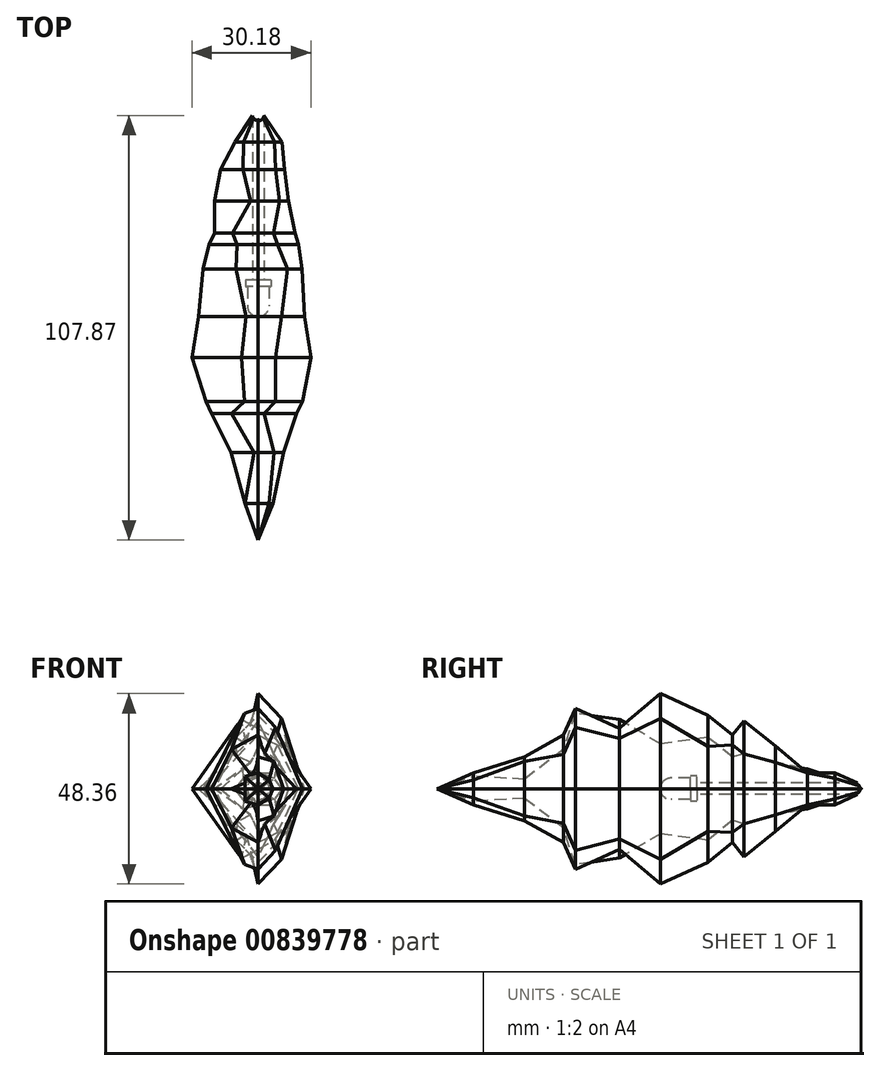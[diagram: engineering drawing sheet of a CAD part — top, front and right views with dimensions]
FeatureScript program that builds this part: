
annotation { "Feature Type Name" : "Feature", "Feature Type Description" : "" }
export const myFeature = defineFeature(function(context is Context, id is Id, definition is map)
    precondition{}
    {
        {
            var Q0;
            Q0=qCreatedBy(makeId("Right.planeOp"),FACE);
            var sketch = newSketch(context, id + "F0", { "sketchPlane" : qUnion([Q0])});
            skLineSegment(sketch, "E0", {"start": v(-34.53, 8.11) * mm, "end": v(-24.64, 13.67) * mm});
            skLineSegment(sketch, "E1", {"start": v(-24.64, 13.67) * mm, "end": v(-21.55, 20.44) * mm});
            skLineSegment(sketch, "E2", {"start": v(-21.55, 20.44) * mm, "end": v(-10.37, 15.33) * mm});
            skLineSegment(sketch, "E3", {"start": v(-10.37, 15.33) * mm, "end": v(0, 24.18) * mm});
            skLineSegment(sketch, "E4", {"start": v(0, 24.18) * mm, "end": v(12.06, 18.66) * mm});
            skLineSegment(sketch, "E5", {"start": v(12.06, 18.66) * mm, "end": v(18.3, 13.67) * mm});
            skLineSegment(sketch, "E6", {"start": v(18.3, 13.67) * mm, "end": v(21.2, 17.3) * mm});
            skLineSegment(sketch, "E7", {"start": v(21.2, 17.3) * mm, "end": v(29.3, 10.81) * mm});
            skLineSegment(sketch, "E8", {"start": v(-34.53, 8.11) * mm, "end": v(-47.5, 4.06) * mm});
            skLineSegment(sketch, "E9", {"start": v(-47.5, 4.06) * mm, "end": v(-56.78, 0) * mm});
            skLineSegment(sketch, "E10", {"start": v(44.35, 4.06) * mm, "end": v(53.22, 0) * mm});
            skLineSegment(sketch, "E11", {"start": v(29.3, 10.81) * mm, "end": v(37.37, 4.06) * mm});
            skLineSegment(sketch, "E12", {"start": v(-56.78, 0) * mm, "end": v(53.22, 0) * mm});
            skLineSegment(sketch, "E13", {"start": v(44.35, 4.06) * mm, "end": v(37.37, 4.06) * mm});
            skSolve(sketch);
        }
        {
            var Q0;
            Q0=sQuery(id+"F0.wireOp",VERTEX,"E10.start");
            var Q1;
            Q1=sQuery(id+"F0.wireOp",EDGE,"E12");
            cPlane(context, id + "F1", {"entities" : qUnion([Q0, Q1]), "cplaneType" : CPlaneType.LINE_POINT, "offset" : 25 * mm, "width" : 150 * mm, "height" : 150 * mm});
        }
        {
            var Q0;
            Q0=sQuery(id+"F0.wireOp",VERTEX,"E11.end");
            var Q1;
            Q1=sQuery(id+"F0.wireOp",EDGE,"E12");
            cPlane(context, id + "F2", {"entities" : qUnion([Q0, Q1]), "cplaneType" : CPlaneType.LINE_POINT, "offset" : 25 * mm, "width" : 150 * mm, "height" : 150 * mm});
        }
        {
            var Q0;
            Q0=sQuery(id+"F0.wireOp",VERTEX,"E7.end");
            var Q1;
            Q1=sQuery(id+"F0.wireOp",EDGE,"E12");
            cPlane(context, id + "F3", {"entities" : qUnion([Q0, Q1]), "cplaneType" : CPlaneType.LINE_POINT, "offset" : 25 * mm, "width" : 150 * mm, "height" : 150 * mm});
        }
        {
            var Q0;
            Q0=sQuery(id+"F0.wireOp",VERTEX,"E6.end");
            var Q1;
            Q1=sQuery(id+"F0.wireOp",EDGE,"E12");
            cPlane(context, id + "F4", {"entities" : qUnion([Q0, Q1]), "cplaneType" : CPlaneType.LINE_POINT, "offset" : 25 * mm, "width" : 150 * mm, "height" : 150 * mm});
        }
        {
            var Q0;
            Q0=sQuery(id+"F0.wireOp",VERTEX,"E5.end");
            var Q1;
            Q1=sQuery(id+"F0.wireOp",EDGE,"E12");
            cPlane(context, id + "F5", {"entities" : qUnion([Q0, Q1]), "cplaneType" : CPlaneType.LINE_POINT, "offset" : 25 * mm, "width" : 150 * mm, "height" : 150 * mm});
        }
        {
            var Q0;
            Q0=sQuery(id+"F0.wireOp",VERTEX,"E4.end");
            var Q1;
            Q1=sQuery(id+"F0.wireOp",EDGE,"E12");
            cPlane(context, id + "F6", {"entities" : qUnion([Q0, Q1]), "cplaneType" : CPlaneType.LINE_POINT, "offset" : 25 * mm, "width" : 150 * mm, "height" : 150 * mm});
        }
        {
            var Q0;
            Q0=sQuery(id+"F0.wireOp",VERTEX,"E3.end");
            var Q1;
            Q1=sQuery(id+"F0.wireOp",EDGE,"E12");
            cPlane(context, id + "F7", {"entities" : qUnion([Q0, Q1]), "cplaneType" : CPlaneType.LINE_POINT, "offset" : 25 * mm, "width" : 150 * mm, "height" : 150 * mm});
        }
        {
            var Q0;
            Q0=sQuery(id+"F0.wireOp",VERTEX,"E2.end");
            var Q1;
            Q1=sQuery(id+"F0.wireOp",EDGE,"E12");
            cPlane(context, id + "F8", {"entities" : qUnion([Q0, Q1]), "cplaneType" : CPlaneType.LINE_POINT, "offset" : 25 * mm, "width" : 150 * mm, "height" : 150 * mm});
        }
        {
            var Q0;
            Q0=sQuery(id+"F0.wireOp",VERTEX,"E1.end");
            var Q1;
            Q1=sQuery(id+"F0.wireOp",EDGE,"E12");
            cPlane(context, id + "F9", {"entities" : qUnion([Q0, Q1]), "cplaneType" : CPlaneType.LINE_POINT, "offset" : 25 * mm, "width" : 150 * mm, "height" : 150 * mm});
        }
        {
            var Q0;
            Q0=sQuery(id+"F0.wireOp",VERTEX,"E0.end");
            var Q1;
            Q1=sQuery(id+"F0.wireOp",EDGE,"E12");
            cPlane(context, id + "F10", {"entities" : qUnion([Q0, Q1]), "cplaneType" : CPlaneType.LINE_POINT, "offset" : 25 * mm, "width" : 150 * mm, "height" : 150 * mm});
        }
        {
            var Q0;
            Q0=sQuery(id+"F0.wireOp",VERTEX,"E0.start");
            var Q1;
            Q1=sQuery(id+"F0.wireOp",EDGE,"E12");
            cPlane(context, id + "F11", {"entities" : qUnion([Q0, Q1]), "cplaneType" : CPlaneType.LINE_POINT, "offset" : 25 * mm, "width" : 150 * mm, "height" : 150 * mm});
        }
        {
            var Q0;
            Q0=sQuery(id+"F0.wireOp",VERTEX,"E8.end");
            var Q1;
            Q1=sQuery(id+"F0.wireOp",EDGE,"E12");
            cPlane(context, id + "F12", {"entities" : qUnion([Q0, Q1]), "cplaneType" : CPlaneType.LINE_POINT, "offset" : 25 * mm, "width" : 150 * mm, "height" : 150 * mm});
        }
        {
            var Q0;
            Q0=qCreatedBy(id+"F1.planeOp",FACE);
            var sketch = newSketch(context, id + "F13", { "sketchPlane" : qUnion([Q0])});
            skPoint(sketch, "E14.0", {"position": v(0, 4.06) * mm});
            skLineSegment(sketch, "E15", {"start": v(0, 4.06) * mm, "end": v(3.8, 2.78) * mm});
            skLineSegment(sketch, "E16", {"start": v(3.8, 2.78) * mm, "end": v(5.94, 0) * mm});
            skLineSegment(sketch, "E17", {"start": v(5.94, 0) * mm, "end": v(-6.04, 0) * mm});
            skLineSegment(sketch, "E18", {"start": v(-6.04, 0) * mm, "end": v(-4.09, 2.6) * mm});
            skLineSegment(sketch, "E19", {"start": v(-4.09, 2.6) * mm, "end": v(0, 4.06) * mm});
            skSolve(sketch);
        }
        {
            var Q0;
            Q0=qCreatedBy(id+"F2.planeOp",FACE);
            var sketch = newSketch(context, id + "F14", { "sketchPlane" : qUnion([Q0])});
            skPoint(sketch, "E20.0", {"position": v(0, 4.06) * mm});
            skLineSegment(sketch, "E21", {"start": v(0, 4.06) * mm, "end": v(-4.45, 4.06) * mm});
            skLineSegment(sketch, "E22", {"start": v(-4.45, 4.06) * mm, "end": v(-6.68, 0) * mm});
            skLineSegment(sketch, "E23", {"start": v(-6.68, 0) * mm, "end": v(9.54, 0) * mm});
            skLineSegment(sketch, "E24", {"start": v(9.54, 0) * mm, "end": v(3.9, 5.05) * mm});
            skLineSegment(sketch, "E25", {"start": v(3.9, 5.05) * mm, "end": v(0, 4.06) * mm});
            skSolve(sketch);
        }
        {
            var Q0;
            Q0=qCreatedBy(id+"F3.planeOp",FACE);
            var sketch = newSketch(context, id + "F15", { "sketchPlane" : qUnion([Q0])});
            skPoint(sketch, "E26", {"position": v(0, 10.87) * mm});
            skLineSegment(sketch, "E27", {"start": v(-7.66, 0) * mm, "end": v(-5.4, 6.67) * mm});
            skLineSegment(sketch, "E28", {"start": v(-5.4, 6.67) * mm, "end": v(0, 10.87) * mm});
            skLineSegment(sketch, "E29", {"start": v(0, 10.87) * mm, "end": v(1.92, 6.67) * mm});
            skLineSegment(sketch, "E30", {"start": v(1.92, 6.67) * mm, "end": v(11.06, 0) * mm});
            skLineSegment(sketch, "E31", {"start": v(11.06, 0) * mm, "end": v(-7.66, 0) * mm});
            skSolve(sketch);
        }
        {
            var Q0;
            Q0=qCreatedBy(id+"F4.planeOp",FACE);
            var sketch = newSketch(context, id + "F16", { "sketchPlane" : qUnion([Q0])});
            skPoint(sketch, "E32.0", {"position": v(0, 17.3) * mm});
            skLineSegment(sketch, "E33", {"start": v(-9.31, 0) * mm, "end": v(-3.87, 8.9) * mm});
            skLineSegment(sketch, "E34", {"start": v(-3.87, 8.9) * mm, "end": v(0, 17.3) * mm});
            skLineSegment(sketch, "E35", {"start": v(0, 17.3) * mm, "end": v(6.54, 8.9) * mm});
            skLineSegment(sketch, "E36", {"start": v(6.54, 8.9) * mm, "end": v(11.15, 0) * mm});
            skLineSegment(sketch, "E37", {"start": v(11.15, 0) * mm, "end": v(-9.31, 0) * mm});
            skSolve(sketch);
        }
        {
            var Q0;
            Q0=qCreatedBy(id+"F5.planeOp",FACE);
            var sketch = newSketch(context, id + "F17", { "sketchPlane" : qUnion([Q0])});
            skPoint(sketch, "E38.0", {"position": v(0, 13.67) * mm});
            skLineSegment(sketch, "E39", {"start": v(0, 13.67) * mm, "end": v(-4.93, 11.1) * mm});
            skLineSegment(sketch, "E40", {"start": v(-4.93, 11.1) * mm, "end": v(-10.2, 0) * mm});
            skLineSegment(sketch, "E41", {"start": v(-10.2, 0) * mm, "end": v(12.55, 0) * mm});
            skLineSegment(sketch, "E42", {"start": v(12.55, 0) * mm, "end": v(5.43, 8.08) * mm});
            skLineSegment(sketch, "E43", {"start": v(5.43, 8.08) * mm, "end": v(0, 13.67) * mm});
            skSolve(sketch);
        }
        {
            var Q0;
            Q0=qCreatedBy(id+"F6.planeOp",FACE);
            var sketch = newSketch(context, id + "F18", { "sketchPlane" : qUnion([Q0])});
            skPoint(sketch, "E44.0", {"position": v(0, 18.66) * mm});
            skLineSegment(sketch, "E45", {"start": v(0, 18.66) * mm, "end": v(-7.43, 10.78) * mm});
            skLineSegment(sketch, "E46", {"start": v(-7.43, 10.78) * mm, "end": v(-11.12, 0) * mm});
            skLineSegment(sketch, "E47", {"start": v(-11.12, 0) * mm, "end": v(14.03, 0) * mm});
            skLineSegment(sketch, "E48", {"start": v(14.03, 0) * mm, "end": v(5.59, 13.07) * mm});
            skLineSegment(sketch, "E49", {"start": v(5.59, 13.07) * mm, "end": v(0, 18.66) * mm});
            skSolve(sketch);
        }
        {
            var Q0;
            Q0=qCreatedBy(id+"F7.planeOp",FACE);
            var sketch = newSketch(context, id + "F19", { "sketchPlane" : qUnion([Q0])});
            skPoint(sketch, "E50.0", {"position": v(0, 24.18) * mm});
            skLineSegment(sketch, "E51", {"start": v(0, 24.18) * mm, "end": v(-5.97, 17.9) * mm});
            skLineSegment(sketch, "E52", {"start": v(-5.97, 17.9) * mm, "end": v(-11.7, 0) * mm});
            skLineSegment(sketch, "E53", {"start": v(-11.7, 0) * mm, "end": v(15.17, 0) * mm});
            skLineSegment(sketch, "E54", {"start": v(15.17, 0) * mm, "end": v(3.05, 11.41) * mm});
            skLineSegment(sketch, "E55", {"start": v(3.05, 11.41) * mm, "end": v(0, 24.18) * mm});
            skSolve(sketch);
        }
        {
            var Q0;
            Q0=qCreatedBy(id+"F8.planeOp",FACE);
            var sketch = newSketch(context, id + "F20", { "sketchPlane" : qUnion([Q0])});
            skPoint(sketch, "E56.0", {"position": v(0, 15.33) * mm});
            skLineSegment(sketch, "E57", {"start": v(0, 15.33) * mm, "end": v(-4.33, 12.79) * mm});
            skLineSegment(sketch, "E58", {"start": v(-4.33, 12.79) * mm, "end": v(-13.36, 0) * mm});
            skLineSegment(sketch, "E59", {"start": v(-13.36, 0) * mm, "end": v(16.82, 0) * mm});
            skLineSegment(sketch, "E60", {"start": v(16.82, 0) * mm, "end": v(4.27, 17.61) * mm});
            skLineSegment(sketch, "E61", {"start": v(4.27, 17.61) * mm, "end": v(0, 15.33) * mm});
            skSolve(sketch);
        }
        {
            var Q0;
            Q0=qCreatedBy(id+"F9.planeOp",FACE);
            var sketch = newSketch(context, id + "F21", { "sketchPlane" : qUnion([Q0])});
            skPoint(sketch, "E62.0", {"position": v(0, 20.44) * mm});
            skLineSegment(sketch, "E63", {"start": v(0, 20.44) * mm, "end": v(-4.37, 15.62) * mm});
            skLineSegment(sketch, "E64", {"start": v(-4.37, 15.62) * mm, "end": v(-11.3, 0) * mm});
            skLineSegment(sketch, "E65", {"start": v(-11.3, 0) * mm, "end": v(13.23, 0) * mm});
            skLineSegment(sketch, "E66", {"start": v(13.23, 0) * mm, "end": v(3.43, 19.2) * mm});
            skLineSegment(sketch, "E67", {"start": v(3.43, 19.2) * mm, "end": v(0, 20.44) * mm});
            skSolve(sketch);
        }
        {
            var Q0;
            Q0=qCreatedBy(id+"F10.planeOp",FACE);
            var sketch = newSketch(context, id + "F22", { "sketchPlane" : qUnion([Q0])});
            skPoint(sketch, "E68.0", {"position": v(0, 13.67) * mm});
            skLineSegment(sketch, "E69", {"start": v(0, 13.67) * mm, "end": v(-1.48, 8.77) * mm});
            skLineSegment(sketch, "E70", {"start": v(-1.48, 8.77) * mm, "end": v(-9.71, 0) * mm});
            skLineSegment(sketch, "E71", {"start": v(-9.71, 0) * mm, "end": v(11.92, 0) * mm});
            skLineSegment(sketch, "E72", {"start": v(11.92, 0) * mm, "end": v(6.81, 9.97) * mm});
            skLineSegment(sketch, "E73", {"start": v(6.81, 9.97) * mm, "end": v(0, 13.67) * mm});
            skSolve(sketch);
        }
        {
            var Q0;
            Q0=qCreatedBy(id+"F11.planeOp",FACE);
            var sketch = newSketch(context, id + "F23", { "sketchPlane" : qUnion([Q0])});
            skPoint(sketch, "E74.0", {"position": v(0, 8.11) * mm});
            skLineSegment(sketch, "E75", {"start": v(0, 8.11) * mm, "end": v(-4.02, 6.92) * mm});
            skLineSegment(sketch, "E76", {"start": v(-4.02, 6.92) * mm, "end": v(-6.36, 0) * mm});
            skLineSegment(sketch, "E77", {"start": v(-6.36, 0) * mm, "end": v(6.91, 0) * mm});
            skLineSegment(sketch, "E78", {"start": v(6.91, 0) * mm, "end": v(1.09, 2.38) * mm});
            skLineSegment(sketch, "E79", {"start": v(1.09, 2.38) * mm, "end": v(0, 8.11) * mm});
            skSolve(sketch);
        }
        {
            var Q0;
            Q0=qCreatedBy(id+"F12.planeOp",FACE);
            var sketch = newSketch(context, id + "F24", { "sketchPlane" : qUnion([Q0])});
            skPoint(sketch, "E80.0", {"position": v(0, 4.06) * mm});
            skLineSegment(sketch, "E81", {"start": v(0, 4.06) * mm, "end": v(-2.75, 2.31) * mm});
            skLineSegment(sketch, "E82", {"start": v(-2.75, 2.31) * mm, "end": v(-3.73, 0) * mm});
            skLineSegment(sketch, "E83", {"start": v(-3.73, 0) * mm, "end": v(3.32, 0) * mm});
            skLineSegment(sketch, "E84", {"start": v(3.32, 0) * mm, "end": v(3.32, 3.2) * mm});
            skLineSegment(sketch, "E85", {"start": v(3.32, 3.2) * mm, "end": v(0, 4.06) * mm});
            skSolve(sketch);
        }
        {
            var Q0;
            Q0=sQuery(id+"F0.wireOp",VERTEX,"E10.end");
            var Q1;
            Q1=makeQuery(id+"F13.imprint","IMPRINT",FACE,{"disambiguationData":[TD([[makeQuery(id+"F13.imprint","IMPRINT",EDGE,{"derivedFrom":sQuery(id+"F13.wireOp",EDGE,"E15")}),-1.0]])]});
            loft(context, id + "F25", {"sheetProfilesArray" : [{ "sheetProfileEntities" : qUnion([Q0]) }, { "sheetProfileEntities" : qUnion([Q1]) }]});
        }
        {
            var Q1;
            Q1 = qSketchRegion(id + "F13", true);
            var Q2;
            Q2 = qSketchRegion(id + "F14", true);
            loft(context, id + "F26", {"operationType" : NewBodyOperationType.ADD, "sheetProfilesArray" : [{ "sheetProfileEntities" : qUnion([Q1]) }, { "sheetProfileEntities" : qUnion([Q2]) }]});
        }
        {
            var Q1;
            Q1 = qSketchRegion(id + "F14", true);
            var Q2;
            Q2 = qSketchRegion(id + "F15", true);
            loft(context, id + "F27", {"operationType" : NewBodyOperationType.ADD, "sheetProfilesArray" : [{ "sheetProfileEntities" : qUnion([Q1]) }, { "sheetProfileEntities" : qUnion([Q2]) }]});
        }
        {
            var Q1;
            Q1 = qSketchRegion(id + "F15", true);
            var Q2;
            Q2 = qSketchRegion(id + "F16", true);
            loft(context, id + "F28", {"operationType" : NewBodyOperationType.ADD, "sheetProfilesArray" : [{ "sheetProfileEntities" : qUnion([Q1]) }, { "sheetProfileEntities" : qUnion([Q2]) }]});
        }
        {
            var Q1;
            Q1 = qSketchRegion(id + "F16", true);
            var Q2;
            Q2 = qSketchRegion(id + "F17", true);
            loft(context, id + "F29", {"operationType" : NewBodyOperationType.ADD, "sheetProfilesArray" : [{ "sheetProfileEntities" : qUnion([Q1]) }, { "sheetProfileEntities" : qUnion([Q2]) }]});
        }
        {
            var Q1;
            Q1 = qSketchRegion(id + "F17", true);
            var Q2;
            Q2 = qSketchRegion(id + "F18", true);
            loft(context, id + "F30", {"operationType" : NewBodyOperationType.ADD, "sheetProfilesArray" : [{ "sheetProfileEntities" : qUnion([Q1]) }, { "sheetProfileEntities" : qUnion([Q2]) }]});
        }
        {
            var Q1;
            Q1 = qSketchRegion(id + "F18", true);
            var Q2;
            Q2 = qSketchRegion(id + "F19", true);
            loft(context, id + "F31", {"operationType" : NewBodyOperationType.ADD, "sheetProfilesArray" : [{ "sheetProfileEntities" : qUnion([Q1]) }, { "sheetProfileEntities" : qUnion([Q2]) }]});
        }
        {
            var Q1;
            Q1 = qSketchRegion(id + "F19", true);
            var Q2;
            Q2 = qSketchRegion(id + "F20", true);
            loft(context, id + "F32", {"operationType" : NewBodyOperationType.ADD, "sheetProfilesArray" : [{ "sheetProfileEntities" : qUnion([Q1]) }, { "sheetProfileEntities" : qUnion([Q2]) }]});
        }
        {
            var Q1;
            Q1 = qSketchRegion(id + "F20", true);
            var Q2;
            Q2 = qSketchRegion(id + "F21", true);
            loft(context, id + "F33", {"operationType" : NewBodyOperationType.ADD, "sheetProfilesArray" : [{ "sheetProfileEntities" : qUnion([Q1]) }, { "sheetProfileEntities" : qUnion([Q2]) }]});
        }
        {
            var Q1;
            Q1 = qSketchRegion(id + "F21", true);
            var Q2;
            Q2 = qSketchRegion(id + "F22", true);
            loft(context, id + "F34", {"operationType" : NewBodyOperationType.ADD, "sheetProfilesArray" : [{ "sheetProfileEntities" : qUnion([Q1]) }, { "sheetProfileEntities" : qUnion([Q2]) }]});
        }
        {
            var Q1;
            Q1 = qSketchRegion(id + "F22", true);
            var Q2;
            Q2 = qSketchRegion(id + "F23", true);
            loft(context, id + "F35", {"operationType" : NewBodyOperationType.ADD, "sheetProfilesArray" : [{ "sheetProfileEntities" : qUnion([Q1]) }, { "sheetProfileEntities" : qUnion([Q2]) }]});
        }
        {
            var Q1;
            Q1 = qSketchRegion(id + "F23", true);
            var Q2;
            Q2 = qSketchRegion(id + "F24", true);
            loft(context, id + "F36", {"operationType" : NewBodyOperationType.ADD, "sheetProfilesArray" : [{ "sheetProfileEntities" : qUnion([Q1]) }, { "sheetProfileEntities" : qUnion([Q2]) }]});
        }
        {
            var Q1;
            Q1=sQuery(id+"F0.wireOp",VERTEX,"E9.end");
            var Q2;
            Q2 = qSketchRegion(id + "F24", true);
            loft(context, id + "F37", {"operationType" : NewBodyOperationType.ADD, "sheetProfilesArray" : [{ "sheetProfileEntities" : qUnion([Q1]) }, { "sheetProfileEntities" : qUnion([Q2]) }]});
        }
        {
            var Q0;
            Q0=qCreatedBy(makeId("Right.planeOp"),FACE);
            var sketch = newSketch(context, id + "F38", { "sketchPlane" : qUnion([Q0])});
            skLineSegment(sketch, "E86", {"start": v(9.3, 0) * mm, "end": v(9.3, 3.25) * mm});
            skLineSegment(sketch, "E87", {"start": v(9.3, 3.25) * mm, "end": v(7.6, 3.25) * mm});
            skLineSegment(sketch, "E88", {"start": v(7.6, 3.25) * mm, "end": v(7.6, 2.75) * mm});
            skLineSegment(sketch, "E89", {"start": v(7.6, 2.75) * mm, "end": v(2.75, 2.75) * mm});
            skArc(sketch, "E90", {"start": v(2.75, 2.75) * mm, "mid": v(0.8, 1.94) * mm, "end": v(0, 0) * mm});
            skLineSegment(sketch, "E91", {"start": v(9.3, 0) * mm, "end": v(0, 0) * mm});
            skLineSegment(sketch, "E92.bottom", {"start": v(9.3, 0) * mm, "end": v(54.08, 0) * mm});
            skLineSegment(sketch, "E92.top", {"start": v(9.3, 1.45) * mm, "end": v(54.08, 1.45) * mm});
            skLineSegment(sketch, "E92.left", {"start": v(9.3, 0) * mm, "end": v(9.3, 1.45) * mm});
            skLineSegment(sketch, "E92.right", {"start": v(54.08, 0) * mm, "end": v(54.08, 1.45) * mm});
            skSolve(sketch);
        }
        {
            var Q0;
            Q0=makeQuery(id+"F38.imprint","IMPRINT",FACE,{"disambiguationData":[TD([[makeQuery(id+"F38.imprint","IMPRINT",EDGE,{"derivedFrom":sQuery(id+"F38.wireOp",EDGE,"E92.bottom")}),1.0]])]});
            var Q1;
            Q1=makeQuery(id+"F38.imprint","IMPRINT",FACE,{"disambiguationData":[TD([[makeQuery(id+"F38.imprint","IMPRINT",EDGE,{"derivedFrom":sQuery(id+"F38.wireOp",EDGE,"E86")}),1.0]])]});
            var Q2;
            Q2=sQuery(id+"F38.wireOp",EDGE,"E91");
            revolve(context, id + "F39", {"operationType" : NewBodyOperationType.REMOVE, "surfaceOperationType" : NewSurfaceOperationType.NEW, "entities" : qUnion([Q0, Q1]), "axis" : qUnion([Q2]), "revolveType" : RevolveType.FULL, "oppositeDirection" : true});
        }
        {
            var Q0;
            Q0=makeQuery(id+"F25.opLoft","SWEPT_BODY",BODY,{"disambiguationData":[OSD([sQuery(id+"F0.wireOp",VERTEX,"E10.end"),makeQuery(id+"F13.imprint","IMPRINT",FACE,{"disambiguationData":[TD([[makeQuery(id+"F13.imprint","IMPRINT",EDGE,{"derivedFrom":sQuery(id+"F13.wireOp",EDGE,"E15")}),-1.0]])]})])]});
            var Q1;
            {var subQ0=sQuery(id+"F24.wireOp",EDGE,"E84");var subQ1=sQuery(id+"F24.wireOp",EDGE,"E83");var subQ2=sQuery(id+"F24.wireOp",EDGE,"E82");var subQ3=sQuery(id+"F23.wireOp",EDGE,"E78");var subQ4=sQuery(id+"F23.wireOp",EDGE,"E77");var subQ5=sQuery(id+"F23.wireOp",EDGE,"E76");var subQ6=sQuery(id+"F22.wireOp",EDGE,"E72");var subQ7=sQuery(id+"F22.wireOp",EDGE,"E71");var subQ8=sQuery(id+"F22.wireOp",EDGE,"E70");var subQ9=sQuery(id+"F21.wireOp",EDGE,"E66");var subQ10=sQuery(id+"F21.wireOp",EDGE,"E65");var subQ11=sQuery(id+"F21.wireOp",EDGE,"E64");var subQ12=sQuery(id+"F20.wireOp",EDGE,"E60");var subQ13=sQuery(id+"F20.wireOp",EDGE,"E59");var subQ14=sQuery(id+"F20.wireOp",EDGE,"E58");var subQ15=sQuery(id+"F19.wireOp",EDGE,"E54");var subQ16=sQuery(id+"F19.wireOp",EDGE,"E53");var subQ17=sQuery(id+"F19.wireOp",EDGE,"E52");var subQ18=sQuery(id+"F18.wireOp",EDGE,"E48");var subQ19=sQuery(id+"F18.wireOp",EDGE,"E47");var subQ20=sQuery(id+"F18.wireOp",EDGE,"E46");var subQ21=sQuery(id+"F17.wireOp",EDGE,"E42");var subQ22=sQuery(id+"F17.wireOp",EDGE,"E41");var subQ23=sQuery(id+"F17.wireOp",EDGE,"E40");var subQ24=sQuery(id+"F16.wireOp",EDGE,"E37");var subQ25=sQuery(id+"F16.wireOp",EDGE,"E36");var subQ26=sQuery(id+"F16.wireOp",EDGE,"E33");var subQ27=sQuery(id+"F15.wireOp",EDGE,"E31");var subQ28=sQuery(id+"F15.wireOp",EDGE,"E30");var subQ29=sQuery(id+"F15.wireOp",EDGE,"E27");var subQ30=sQuery(id+"F14.wireOp",EDGE,"E24");var subQ31=sQuery(id+"F14.wireOp",EDGE,"E23");var subQ32=sQuery(id+"F14.wireOp",EDGE,"E22");var subQ33=sQuery(id+"F13.wireOp",EDGE,"E18");var subQ34=sQuery(id+"F13.wireOp",EDGE,"E17");var subQ35=sQuery(id+"F13.wireOp",EDGE,"E16");Q1=makeQuery(id+"F37.boolean.opBoolean","MERGE",FACE,{"derivedFrom":[makeQuery(id+"F36.boolean.opBoolean","MERGE",FACE,{"derivedFrom":[makeQuery(id+"F35.boolean.opBoolean","MERGE",FACE,{"derivedFrom":[makeQuery(id+"F34.boolean.opBoolean","MERGE",FACE,{"derivedFrom":[makeQuery(id+"F33.boolean.opBoolean","MERGE",FACE,{"derivedFrom":[makeQuery(id+"F32.boolean.opBoolean","MERGE",FACE,{"derivedFrom":[makeQuery(id+"F31.boolean.opBoolean","MERGE",FACE,{"derivedFrom":[makeQuery(id+"F30.boolean.opBoolean","MERGE",FACE,{"derivedFrom":[makeQuery(id+"F29.boolean.opBoolean","MERGE",FACE,{"derivedFrom":[makeQuery(id+"F28.boolean.opBoolean","MERGE",FACE,{"derivedFrom":[makeQuery(id+"F27.boolean.opBoolean","MERGE",FACE,{"derivedFrom":[makeQuery(id+"F26.boolean.opBoolean","MERGE",FACE,{"derivedFrom":[makeQuery(id+"F25.opLoft","SWEPT_FACE",FACE,{"disambiguationData":[OSD([subQ35,subQ34,subQ33])]}),makeQuery(id+"F26.opLoft","SWEPT_FACE",FACE,{"disambiguationData":[OSD([subQ35,subQ34,subQ33,subQ32,subQ31,subQ30])]})]}),makeQuery(id+"F27.opLoft","SWEPT_FACE",FACE,{"disambiguationData":[OSD([subQ32,subQ31,subQ30,subQ29,subQ28,subQ27])]})]}),makeQuery(id+"F28.opLoft","SWEPT_FACE",FACE,{"disambiguationData":[OSD([subQ29,subQ28,subQ27,subQ26,subQ25,subQ24])]})]}),makeQuery(id+"F29.opLoft","SWEPT_FACE",FACE,{"disambiguationData":[OSD([subQ26,subQ25,subQ24,subQ23,subQ22,subQ21])]})]}),makeQuery(id+"F30.opLoft","SWEPT_FACE",FACE,{"disambiguationData":[OSD([subQ23,subQ22,subQ21,subQ20,subQ19,subQ18])]})]}),makeQuery(id+"F31.opLoft","SWEPT_FACE",FACE,{"disambiguationData":[OSD([subQ20,subQ19,subQ18,subQ17,subQ16,subQ15])]})]}),makeQuery(id+"F32.opLoft","SWEPT_FACE",FACE,{"disambiguationData":[OSD([subQ17,subQ16,subQ15,subQ14,subQ13,subQ12])]})]}),makeQuery(id+"F33.opLoft","SWEPT_FACE",FACE,{"disambiguationData":[OSD([subQ14,subQ13,subQ12,subQ11,subQ10,subQ9])]})]}),makeQuery(id+"F34.opLoft","SWEPT_FACE",FACE,{"disambiguationData":[OSD([subQ11,subQ10,subQ9,subQ8,subQ7,subQ6])]})]}),makeQuery(id+"F35.opLoft","SWEPT_FACE",FACE,{"disambiguationData":[OSD([subQ8,subQ7,subQ6,subQ5,subQ4,subQ3])]})]}),makeQuery(id+"F36.opLoft","SWEPT_FACE",FACE,{"disambiguationData":[OSD([subQ5,subQ4,subQ3,subQ2,subQ1,subQ0])]})]}),makeQuery(id+"F37.opLoft","SWEPT_FACE",FACE,{"disambiguationData":[OSD([subQ2,subQ1,subQ0])]})]});}
            mirror(context, id + "F40", {"entities" : qUnion([Q0]), "mirrorPlane" : qUnion([Q1])});
        }
    });
